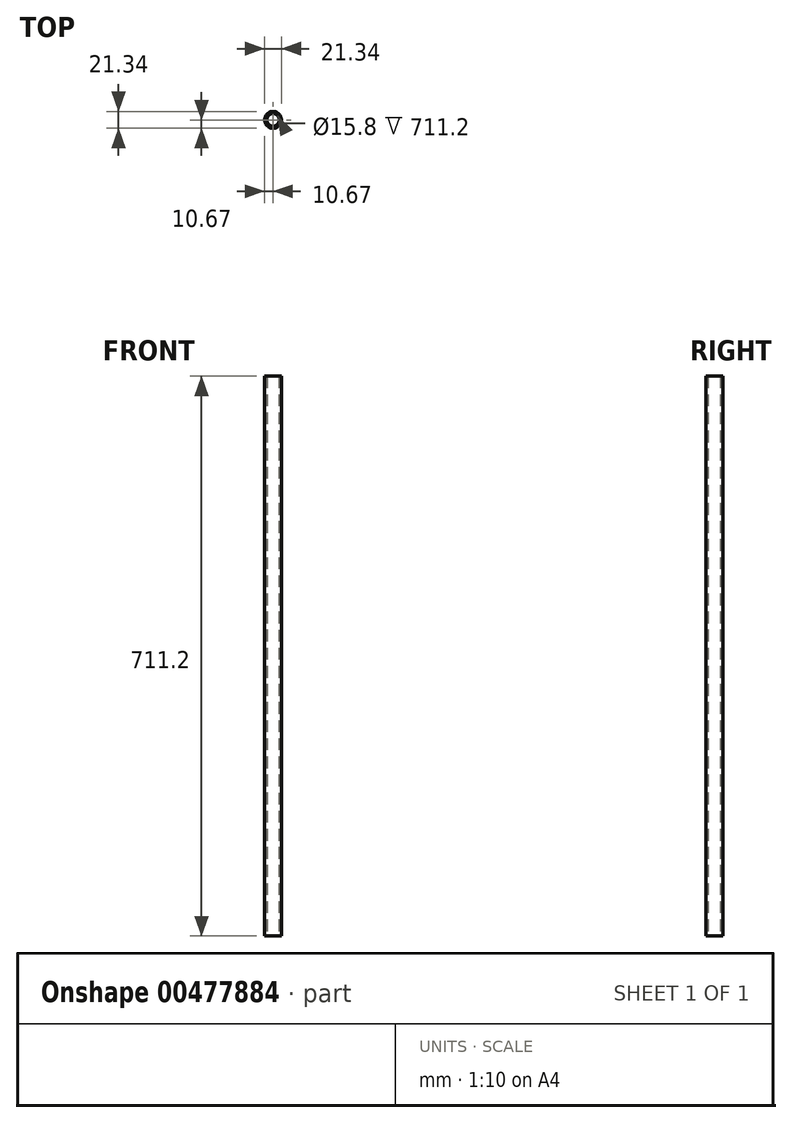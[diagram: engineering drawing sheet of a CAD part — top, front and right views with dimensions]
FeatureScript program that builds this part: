
annotation { "Feature Type Name" : "Feature", "Feature Type Description" : "" }
export const myFeature = defineFeature(function(context is Context, id is Id, definition is map)
    precondition{}
    {
        {
            var Q0;
            Q0=qCreatedBy(makeId("Top.planeOp"),FACE);
            var sketch = newSketch(context, id + "F0", { "sketchPlane" : qUnion([Q0])});
            skCircle(sketch, "E0", {"center": v(0, 0) * mm, "radius": 7.9 * mm});
            skCircle(sketch, "E1", {"center": v(0, 0) * mm, "radius": 10.67 * mm});
            skLineSegment(sketch, "E2", {"start": v(0, 0) * mm, "end": v(0, -7.9) * mm, "construction": true});
            skLineSegment(sketch, "E3", {"start": v(0, -7.9) * mm, "end": v(0, -10.67) * mm, "construction": true});
            skSolve(sketch);
        }
        {
            var Q0;
            Q0=makeQuery(id+"F0.imprint","IMPRINT",FACE,{"disambiguationData":[TD([[makeQuery(id+"F0.imprint","IMPRINT",EDGE,{"derivedFrom":sQuery(id+"F0.wireOp",EDGE,"E0")}),-1.0]])]});
            extrude(context, id + "F1", {"entities" : qUnion([Q0]), "depth" : 711.2 * mm});
        }
    });
